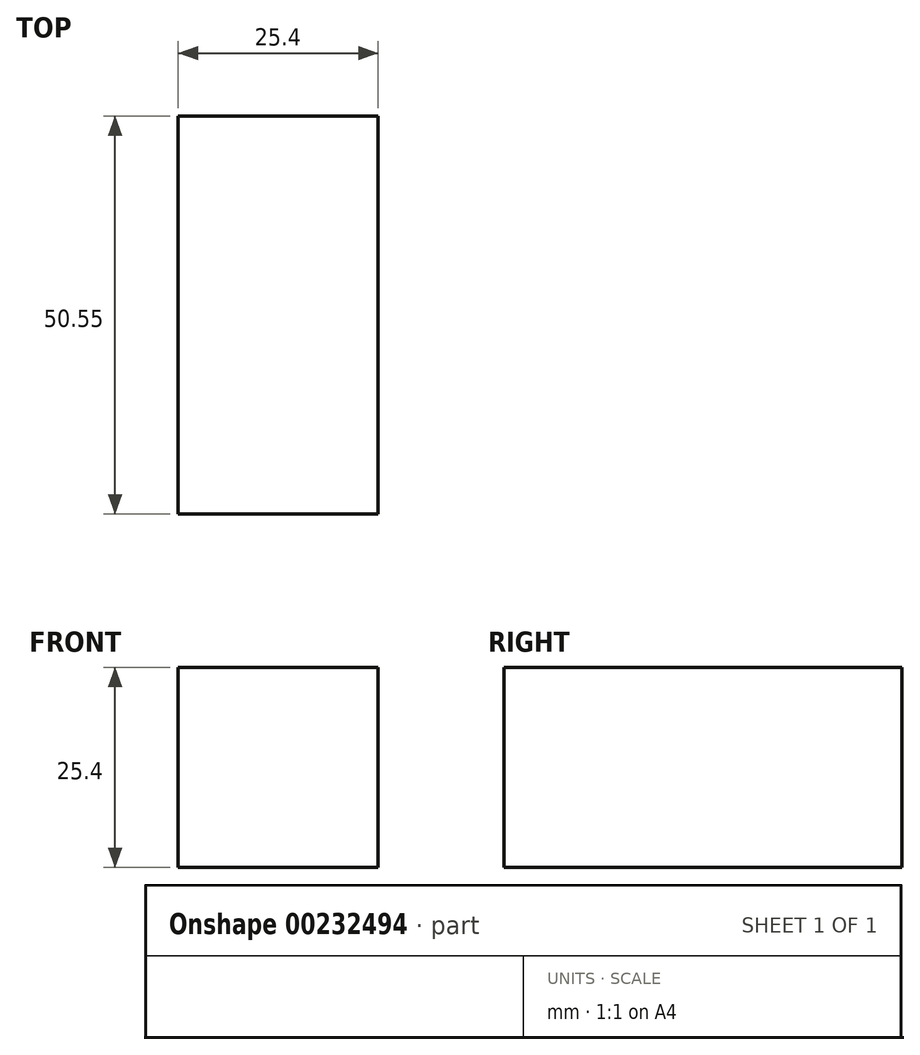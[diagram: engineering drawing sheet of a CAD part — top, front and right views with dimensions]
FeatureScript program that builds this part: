
annotation { "Feature Type Name" : "Feature", "Feature Type Description" : "" }
export const myFeature = defineFeature(function(context is Context, id is Id, definition is map)
    precondition{}
    {
        {
            var Q0;
            Q0=qCreatedBy(makeId("Front.planeOp"),FACE);
            var sketch = newSketch(context, id + "F0", { "sketchPlane" : qUnion([Q0])});
            skLineSegment(sketch, "E0.bottom", {"start": v(-31.3, 4.04) * mm, "end": v(-5.9, 4.04) * mm});
            skLineSegment(sketch, "E0.top", {"start": v(-31.3, -21.36) * mm, "end": v(-5.9, -21.36) * mm});
            skLineSegment(sketch, "E0.left", {"start": v(-31.3, 4.04) * mm, "end": v(-31.3, -21.36) * mm});
            skLineSegment(sketch, "E0.right", {"start": v(-5.9, 4.04) * mm, "end": v(-5.9, -21.36) * mm});
            skSolve(sketch);
        }
        {
            var Q0;
            Q0=makeQuery(id+"F0.imprint","IMPRINT",FACE,{"disambiguationData":[TD([[makeQuery(id+"F0.imprint","IMPRINT",EDGE,{"derivedFrom":sQuery(id+"F0.wireOp",EDGE,"E0.bottom")}),-1.0]])]});
            extrude(context, id + "F1", {"entities" : qUnion([Q0]), "depth" : 50.55 * mm});
        }
    });
